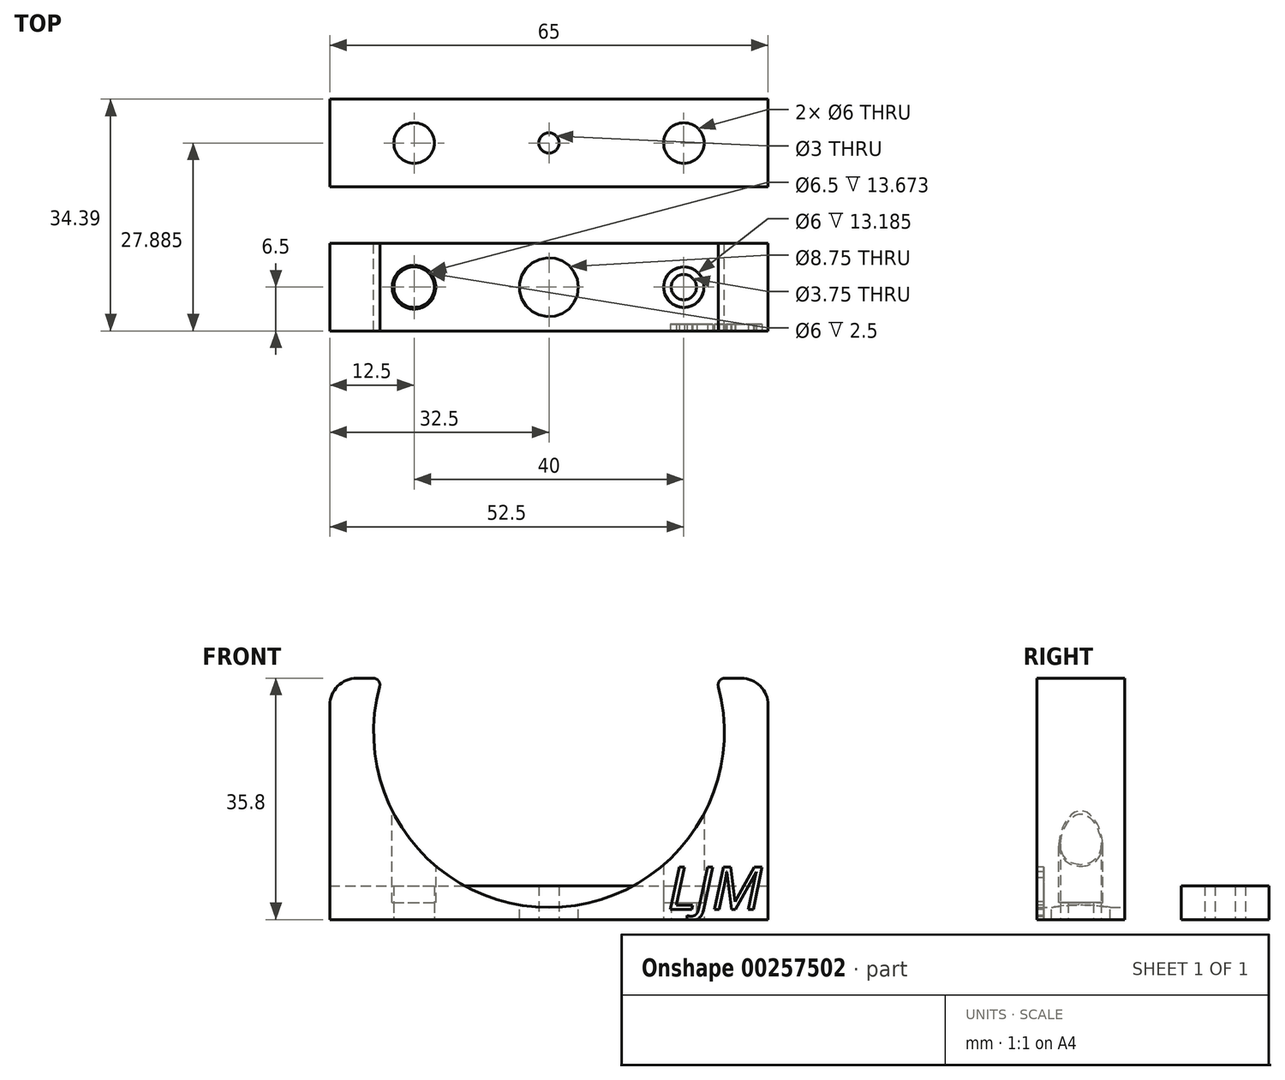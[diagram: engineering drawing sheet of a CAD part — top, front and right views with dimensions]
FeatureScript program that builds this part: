
annotation { "Feature Type Name" : "Feature", "Feature Type Description" : "" }
export const myFeature = defineFeature(function(context is Context, id is Id, definition is map)
    precondition{}
    {
        {
            var Q0;
            Q0=qCreatedBy(makeId("Front.planeOp"),FACE);
            var sketch = newSketch(context, id + "F0", { "sketchPlane" : qUnion([Q0])});
            skLineSegment(sketch, "E0.bottom", {"start": v(32.5, -27.8) * mm, "end": v(-32.5, -27.8) * mm});
            skLineSegment(sketch, "E0.left", {"start": v(32.5, -27.8) * mm, "end": v(32.5, 4) * mm});
            skLineSegment(sketch, "E0.right", {"start": v(-32.5, -27.8) * mm, "end": v(-32.5, 4) * mm});
            skArc(sketch, "E1", {"start": v(-25.11, 6.74) * mm, "mid": v(0, -26) * mm, "end": v(25.11, 6.74) * mm});
            skLineSegment(sketch, "E2", {"start": v(-28.5, 8) * mm, "end": v(-26.08, 8) * mm});
            skPoint(sketch, "E3.orphan", {"position": v(-32.5, -13.29) * mm});
            skPoint(sketch, "E4.orphan", {"position": v(32.5, -13.29) * mm});
            skLineSegment(sketch, "E5.trimOffspring", {"start": v(26.08, 8) * mm, "end": v(28.5, 8) * mm});
            skPoint(sketch, "E6", {"position": v(-32.5, 0) * mm});
            skPoint(sketch, "E7", {"position": v(5.07, -25.5) * mm});
            skPoint(sketch, "E8", {"position": v(0, -27.8) * mm});
            skPoint(sketch, "E9.visualSharp", {"position": v(-32.5, 8) * mm});
            skArc(sketch, "E9.filletArc", {"start": v(-28.5, 8) * mm, "mid": v(-31.33, 6.83) * mm, "end": v(-32.5, 4) * mm});
            skPoint(sketch, "E10.visualSharp", {"position": v(32.5, 8) * mm});
            skArc(sketch, "E10.filletArc", {"start": v(32.5, 4) * mm, "mid": v(31.33, 6.83) * mm, "end": v(28.5, 8) * mm});
            skPoint(sketch, "E11.visualSharp", {"position": v(24.74, 8) * mm});
            skArc(sketch, "E11.filletArc", {"start": v(26.08, 8) * mm, "mid": v(25.28, 7.6) * mm, "end": v(25.11, 6.74) * mm});
            skPoint(sketch, "E12.visualSharp", {"position": v(-24.74, 8) * mm});
            skArc(sketch, "E12.filletArc", {"start": v(-25.11, 6.74) * mm, "mid": v(-25.28, 7.6) * mm, "end": v(-26.08, 8) * mm});
            skSolve(sketch);
        }
        {
            var Q0;
            Q0=qCreatedBy(makeId("Top.planeOp"),FACE);
            var sketch = newSketch(context, id + "F1", { "sketchPlane" : qUnion([Q0])});
            skCircle(sketch, "E13", {"center": v(0, 0) * mm, "radius": 4.38 * mm});
            skCircle(sketch, "E14", {"center": v(20, 0) * mm, "radius": 1.88 * mm});
            skCircle(sketch, "E15.MirrorC", {"center": v(-20, 0) * mm, "radius": 1.88 * mm});
            skCircle(sketch, "E16", {"center": v(20, 0) * mm, "radius": 3.25 * mm});
            skCircle(sketch, "E17.MirrorC", {"center": v(-20, 0) * mm, "radius": 3.25 * mm});
            skSolve(sketch);
        }
        {
            var Q0;
            Q0=makeQuery(id+"F0.imprint","IMPRINT",FACE,{"disambiguationData":[TD([[makeQuery(id+"F0.imprint","IMPRINT",EDGE,{"derivedFrom":sQuery(id+"F0.wireOp",EDGE,"E0.bottom")}),-1.0]])]});
            extrude(context, id + "F2", {"entities" : qUnion([Q0]), "endBound" : BoundingType.SYMMETRIC, "depth" : 13 * mm});
        }
        {
            var Q0;
            Q0=makeQuery(id+"F1.imprint","IMPRINT",FACE,{"disambiguationData":[TD([[makeQuery(id+"F1.imprint","IMPRINT",EDGE,{"derivedFrom":sQuery(id+"F1.wireOp",EDGE,"E13")}),1.0]])]});
            var Q1;
            Q1=makeQuery(id+"F1.imprint","IMPRINT",FACE,{"disambiguationData":[TD([[makeQuery(id+"F1.imprint","IMPRINT",EDGE,{"derivedFrom":sQuery(id+"F1.wireOp",EDGE,"E14")}),1.0]])]});
            var Q2;
            Q2=makeQuery(id+"F1.imprint","IMPRINT",FACE,{"disambiguationData":[TD([[makeQuery(id+"F1.imprint","IMPRINT",EDGE,{"derivedFrom":sQuery(id+"F1.wireOp",EDGE,"E15.MirrorC")}),-1.0]])]});
            var Q3;
            Q3=sQuery(id+"F1.wireOp",EDGE,"E13");
            extrude(context, id + "F3", {"entities" : qUnion([Q0, Q1, Q2]), "operationType" : NewBodyOperationType.REMOVE, "surfaceEntities" : qUnion([Q3]), "endBound" : BoundingType.THROUGH_ALL, "oppositeDirection" : true, "depth" : 25 * mm});
        }
        {
            var Q0;
            Q0=makeQuery(id+"F2.opExtrude","SWEPT_FACE",FACE,{"disambiguationData":[OSD([sQuery(id+"F0.wireOp",EDGE,"E0.bottom")])]});
            var sketch = newSketch(context, id + "F4", { "sketchPlane" : qUnion([Q0])});
            skCircle(sketch, "E18", {"center": v(20, 0) * mm, "radius": 3 * mm});
            skCircle(sketch, "E19.MirrorC", {"center": v(-20, 0) * mm, "radius": 3 * mm});
            skCircle(sketch, "E20", {"center": v(20, -21.39) * mm, "radius": 3 * mm});
            skCircle(sketch, "E21.MirrorC", {"center": v(-20, -21.39) * mm, "radius": 3 * mm});
            skLineSegment(sketch, "E22.bottom", {"start": v(-32.5, -14.89) * mm, "end": v(32.5, -14.89) * mm});
            skLineSegment(sketch, "E22.top", {"start": v(-32.5, -27.89) * mm, "end": v(32.5, -27.89) * mm});
            skLineSegment(sketch, "E22.left", {"start": v(-32.5, -14.89) * mm, "end": v(-32.5, -27.89) * mm});
            skLineSegment(sketch, "E22.right", {"start": v(32.5, -14.89) * mm, "end": v(32.5, -27.89) * mm});
            skCircle(sketch, "E23", {"center": v(0, -21.39) * mm, "radius": 1.5 * mm});
            skSolve(sketch);
        }
        {
            var Q0;
            Q0 = qSketchRegion(id + "F4", true);
            extrude(context, id + "F5", {"entities" : qUnion([Q0]), "operationType" : NewBodyOperationType.REMOVE, "oppositeDirection" : true, "depth" : 25 * mm});
        }
        {
            var Q0;
            Q0=makeQuery(id+"F4.imprint","IMPRINT",FACE,{"disambiguationData":[TD([[makeQuery(id+"F4.imprint","IMPRINT",EDGE,{"derivedFrom":sQuery(id+"F4.wireOp",EDGE,"E18")}),1.0]])]});
            var Q1;
            Q1=makeQuery(id+"F4.imprint","IMPRINT",FACE,{"disambiguationData":[TD([[makeQuery(id+"F4.imprint","IMPRINT",EDGE,{"derivedFrom":sQuery(id+"F4.wireOp",EDGE,"E19.MirrorC")}),-1.0]])]});
            extrude(context, id + "F6", {"entities" : qUnion([Q0, Q1]), "operationType" : NewBodyOperationType.ADD, "oppositeDirection" : true, "depth" : 2.5 * mm});
        }
        {
            var Q0;
            Q0=makeQuery(id+"F2.opExtrude","CAP_FACE",FACE,{"disambiguationData":[OSD([sQuery(id+"F0.wireOp",EDGE,"E0.bottom"),sQuery(id+"F0.wireOp",EDGE,"E0.left"),sQuery(id+"F0.wireOp",EDGE,"E0.right"),sQuery(id+"F0.wireOp",EDGE,"E1"),sQuery(id+"F0.wireOp",EDGE,"E2"),sQuery(id+"F0.wireOp",EDGE,"E5.trimOffspring"),sQuery(id+"F0.wireOp",EDGE,"E9.filletArc"),sQuery(id+"F0.wireOp",EDGE,"E10.filletArc")])],"isStart":false});
            var sketch = newSketch(context, id + "F7", { "sketchPlane" : qUnion([Q0])});
            skText(sketch, "E24", { "text": "LJM", "fontName": "OpenSans-Italic.ttf"});
            const initialGuessF7  = {"E24": [0.01763, -0.0263, 1, 0, 0.00636]};
            skSetInitialGuess(sketch, initialGuessF7);
            skSolve(sketch);
        }
        {
            var Q0;
            Q0 = qSketchRegion(id + "F7", true);
            extrude(context, id + "F8", {"entities" : qUnion([Q0]), "operationType" : NewBodyOperationType.REMOVE, "oppositeDirection" : true, "depth" : 1 * mm});
        }
        {
            var Q0;
            Q0=makeQuery(id+"F4.imprint","IMPRINT",FACE,{"disambiguationData":[TD([[makeQuery(id+"F4.imprint","IMPRINT",EDGE,{"derivedFrom":sQuery(id+"F4.wireOp",EDGE,"E20")}),-1.0]])]});
            extrude(context, id + "F9", {"entities" : qUnion([Q0]), "oppositeDirection" : true, "depth" : 5 * mm});
        }
    });
